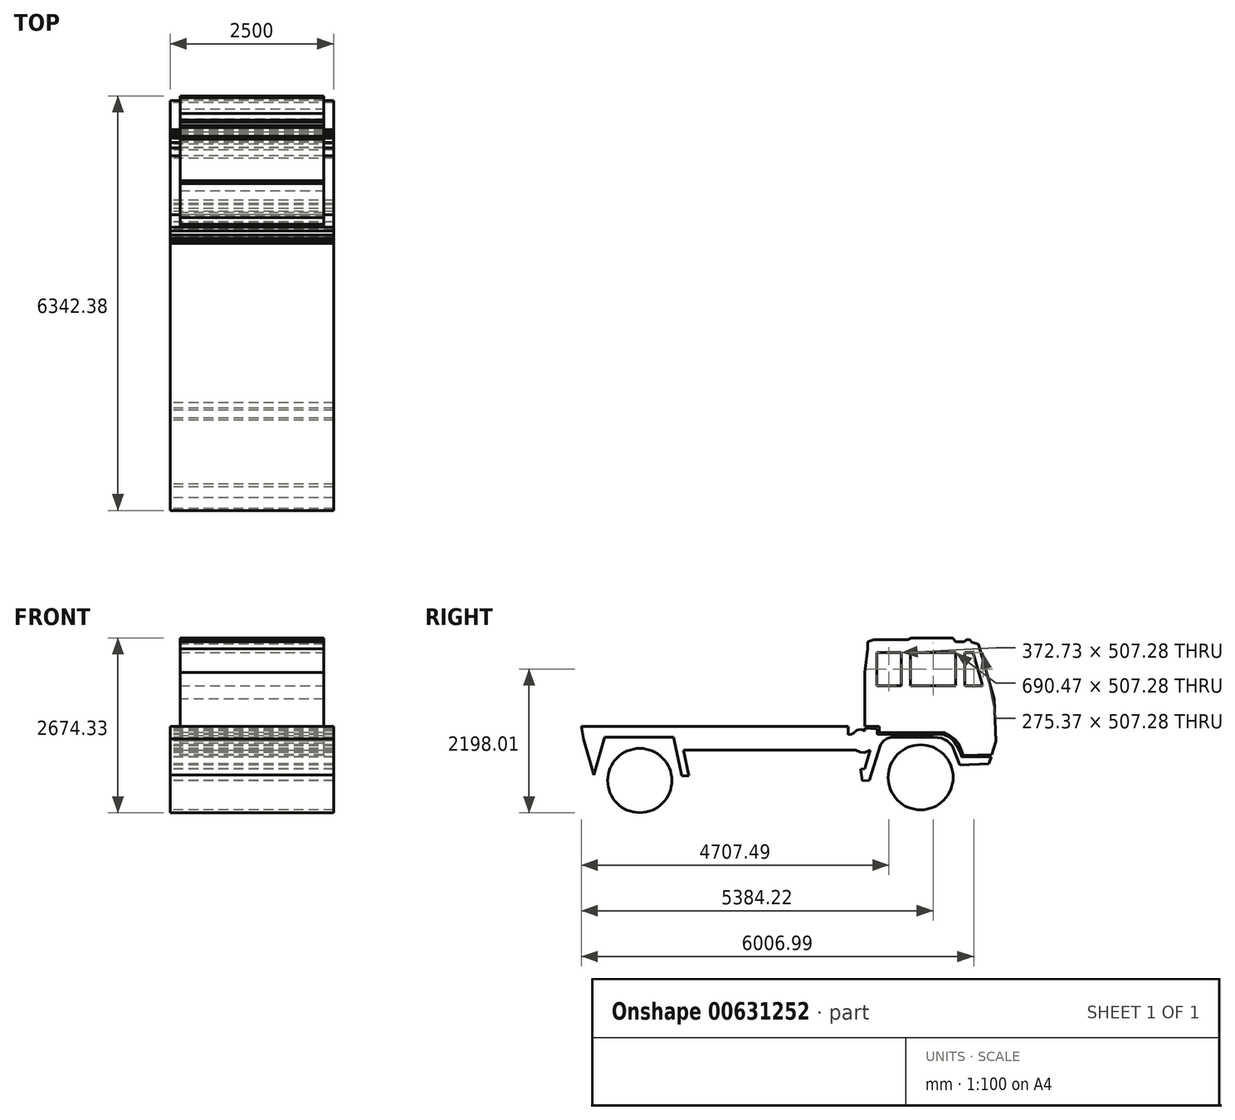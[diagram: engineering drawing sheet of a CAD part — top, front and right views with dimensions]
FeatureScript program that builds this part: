
annotation { "Feature Type Name" : "Feature", "Feature Type Description" : "" }
export const myFeature = defineFeature(function(context is Context, id is Id, definition is map)
    precondition{}
    {
        {
            var Q0;
            Q0=qCreatedBy(makeId("Right.planeOp"),FACE);
            var sketch = newSketch(context, id + "F0", { "sketchPlane" : qUnion([Q0])});
            skLineSegment(sketch, "E0", {"start": v(53.1, 1349.44) * mm, "end": v(53.1, -1350.56) * mm, "construction": true});
            skLineSegment(sketch, "E1", {"start": v(-5310.61, 0) * mm, "end": v(-1224.55, 0) * mm});
            skLineSegment(sketch, "E2", {"start": v(-1224.55, 0) * mm, "end": v(-1224.55, -122.4) * mm});
            skLineSegment(sketch, "E3", {"start": v(-5277.76, -191.96) * mm, "end": v(-5310.61, 0) * mm});
            skLineSegment(sketch, "E4", {"start": v(-974.86, -69.75) * mm, "end": v(-1031.73, -44.93) * mm});
            skLineSegment(sketch, "E5", {"start": v(-1031.73, -44.93) * mm, "end": v(-1096.05, -56.42) * mm});
            skLineSegment(sketch, "E6", {"start": v(-1096.05, -56.42) * mm, "end": v(-1148.89, -109.25) * mm});
            skLineSegment(sketch, "E7", {"start": v(-1148.89, -109.25) * mm, "end": v(-1181.05, -120.74) * mm});
            skLineSegment(sketch, "E8", {"start": v(-1181.05, -120.74) * mm, "end": v(-1224.55, -122.4) * mm});
            skLineSegment(sketch, "E9", {"start": v(962.07, -459.7) * mm, "end": v(927, -569.93) * mm});
            skLineSegment(sketch, "E10", {"start": v(927, -569.93) * mm, "end": v(478.37, -587.13) * mm});
            skLineSegment(sketch, "E11", {"start": v(478.37, -587.13) * mm, "end": v(369.28, -296.74) * mm});
            skLineSegment(sketch, "E12", {"start": v(369.28, -296.74) * mm, "end": v(293.2, -219.28) * mm});
            skLineSegment(sketch, "E13", {"start": v(293.2, -219.28) * mm, "end": v(203.83, -177.57) * mm});
            skLineSegment(sketch, "E14", {"start": v(203.83, -177.57) * mm, "end": v(75.64, -166.68) * mm});
            skLineSegment(sketch, "E15", {"start": v(75.64, -166.68) * mm, "end": v(-564.8, -166.68) * mm});
            skLineSegment(sketch, "E16", {"start": v(-564.8, -166.68) * mm, "end": v(-630.34, -180.55) * mm});
            skLineSegment(sketch, "E17", {"start": v(-630.34, -180.55) * mm, "end": v(-686.95, -222.26) * mm});
            skLineSegment(sketch, "E18", {"start": v(-686.95, -222.26) * mm, "end": v(-731.63, -278.87) * mm});
            skLineSegment(sketch, "E19", {"start": v(-731.63, -278.87) * mm, "end": v(-900.62, -823.83) * mm});
            skLineSegment(sketch, "E20", {"start": v(-900.62, -823.83) * mm, "end": v(-1012.8, -828.13) * mm});
            skLineSegment(sketch, "E21", {"start": v(-1012.8, -828.13) * mm, "end": v(-1035.85, -653.83) * mm});
            skLineSegment(sketch, "E22", {"start": v(-1035.85, -653.83) * mm, "end": v(-974.86, -645.77) * mm});
            skLineSegment(sketch, "E23", {"start": v(-974.86, -645.77) * mm, "end": v(-892.9, -360.2) * mm});
            skLineSegment(sketch, "E24", {"start": v(-892.9, -360.2) * mm, "end": v(-974.86, -398.84) * mm});
            skLineSegment(sketch, "E25", {"start": v(-974.86, -398.84) * mm, "end": v(-1040.88, -393.23) * mm});
            skLineSegment(sketch, "E26", {"start": v(-1040.88, -393.23) * mm, "end": v(-1113.12, -360.2) * mm});
            skLineSegment(sketch, "E27", {"start": v(-1113.12, -360.2) * mm, "end": v(-3746.88, -360.2) * mm});
            skLineSegment(sketch, "E28", {"start": v(-3746.88, -360.2) * mm, "end": v(-3663.76, -753.07) * mm});
            skLineSegment(sketch, "E29", {"start": v(-3663.76, -753.07) * mm, "end": v(-3775.22, -753.07) * mm});
            skLineSegment(sketch, "E30", {"start": v(-3775.22, -753.07) * mm, "end": v(-3899.29, -166.68) * mm});
            skLineSegment(sketch, "E31", {"start": v(-3899.29, -166.68) * mm, "end": v(-4951.76, -166.68) * mm});
            skLineSegment(sketch, "E32", {"start": v(-4951.76, -166.68) * mm, "end": v(-5117.41, -743.82) * mm});
            skLineSegment(sketch, "E33", {"start": v(-5117.41, -743.82) * mm, "end": v(-5277.76, -191.96) * mm});
            skLineSegment(sketch, "E34", {"start": v(-974.86, -24.33) * mm, "end": v(-782.84, -37.54) * mm});
            skLineSegment(sketch, "E35", {"start": v(-782.84, -37.54) * mm, "end": v(-782.84, -116.8) * mm});
            skLineSegment(sketch, "E36", {"start": v(-782.84, -116.8) * mm, "end": v(119.62, -116.8) * mm});
            skLineSegment(sketch, "E37", {"start": v(119.62, -116.8) * mm, "end": v(239.29, -125.04) * mm});
            skLineSegment(sketch, "E38", {"start": v(239.29, -125.04) * mm, "end": v(321.4, -166.68) * mm});
            skLineSegment(sketch, "E39", {"start": v(321.4, -166.68) * mm, "end": v(388.67, -216.02) * mm});
            skLineSegment(sketch, "E40", {"start": v(388.67, -216.02) * mm, "end": v(433.51, -283.28) * mm});
            skLineSegment(sketch, "E41", {"start": v(433.51, -283.28) * mm, "end": v(478.35, -380.44) * mm});
            skLineSegment(sketch, "E42", {"start": v(478.35, -380.44) * mm, "end": v(515.72, -470.12) * mm});
            skLineSegment(sketch, "E43", {"start": v(515.72, -470.12) * mm, "end": v(962.07, -459.7) * mm});
            skLineSegment(sketch, "E44", {"start": v(-974.86, -24.33) * mm, "end": v(-974.86, -69.75) * mm});
            skSolve(sketch);
        }
        {
            var Q0;
            Q0=makeQuery(id+"F0.imprint","IMPRINT",FACE,{"disambiguationData":[TD([[makeQuery(id+"F0.imprint","IMPRINT",EDGE,{"derivedFrom":sQuery(id+"F0.wireOp",EDGE,"E1")}),-1.0]])]});
            var sketch = newSketch(context, id + "F1", { "sketchPlane" : qUnion([Q0])});
            skCircle(sketch, "E45", {"center": v(-4416.91, -827.06) * mm, "radius": 491.64 * mm});
            skCircle(sketch, "E46", {"center": v(-118.33, -776.78) * mm, "radius": 498.02 * mm});
            skSolve(sketch);
        }
        {
            var Q0;
            Q0=makeQuery(id+"F0.imprint","IMPRINT",FACE,{"disambiguationData":[TD([[makeQuery(id+"F0.imprint","IMPRINT",EDGE,{"derivedFrom":sQuery(id+"F0.wireOp",EDGE,"E1")}),-1.0]])]});
            var sketch = newSketch(context, id + "F2", { "sketchPlane" : qUnion([Q0])});
            skLineSegment(sketch, "E47", {"start": v(-974.57, 0) * mm, "end": v(-974.57, 829.4) * mm});
            skLineSegment(sketch, "E48", {"start": v(-974.57, 829.4) * mm, "end": v(-929.28, 1191.21) * mm});
            skLineSegment(sketch, "E49", {"start": v(-929.28, 1191.21) * mm, "end": v(-929.28, 1295.84) * mm});
            skLineSegment(sketch, "E50", {"start": v(-929.28, 1295.84) * mm, "end": v(-832.13, 1325.74) * mm});
            skLineSegment(sketch, "E51", {"start": v(-832.13, 1325.74) * mm, "end": v(-308.98, 1325.74) * mm});
            skLineSegment(sketch, "E52", {"start": v(-308.98, 1325.74) * mm, "end": v(-264.14, 1355.63) * mm});
            skLineSegment(sketch, "E53", {"start": v(-264.14, 1355.63) * mm, "end": v(371.12, 1355.63) * mm});
            skLineSegment(sketch, "E54", {"start": v(371.12, 1355.63) * mm, "end": v(415.96, 1295.84) * mm});
            skLineSegment(sketch, "E55", {"start": v(415.96, 1295.84) * mm, "end": v(550.48, 1295.84) * mm});
            skLineSegment(sketch, "E56", {"start": v(550.48, 1295.84) * mm, "end": v(580.38, 1325.74) * mm});
            skLineSegment(sketch, "E57", {"start": v(580.38, 1325.74) * mm, "end": v(632.7, 1325.74) * mm});
            skLineSegment(sketch, "E58", {"start": v(632.7, 1325.74) * mm, "end": v(662.59, 1288.37) * mm});
            skLineSegment(sketch, "E59", {"start": v(662.59, 1288.37) * mm, "end": v(767.21, 1258.48) * mm});
            skLineSegment(sketch, "E60", {"start": v(767.21, 1258.48) * mm, "end": v(1006.37, 421.44) * mm});
            skLineSegment(sketch, "E61", {"start": v(1006.37, 421.44) * mm, "end": v(1031.77, -227.26) * mm});
            skLineSegment(sketch, "E62", {"start": v(1031.77, -227.26) * mm, "end": v(968.38, -428.96) * mm});
            skLineSegment(sketch, "E63", {"start": v(968.38, -428.96) * mm, "end": v(533.98, -442.83) * mm});
            skLineSegment(sketch, "E64", {"start": v(533.98, -442.83) * mm, "end": v(506.57, -364.01) * mm});
            skLineSegment(sketch, "E65", {"start": v(506.57, -364.01) * mm, "end": v(462.02, -261.21) * mm});
            skLineSegment(sketch, "E66", {"start": v(462.02, -261.21) * mm, "end": v(403.77, -192.68) * mm});
            skLineSegment(sketch, "E67", {"start": v(403.77, -192.68) * mm, "end": v(335.24, -144.7) * mm});
            skLineSegment(sketch, "E68", {"start": v(335.24, -144.7) * mm, "end": v(246.15, -93.3) * mm});
            skLineSegment(sketch, "E69", {"start": v(246.15, -93.3) * mm, "end": v(119.36, -93.3) * mm});
            skLineSegment(sketch, "E70", {"start": v(119.36, -93.3) * mm, "end": v(-750.7, -93.3) * mm});
            skLineSegment(sketch, "E71", {"start": v(-750.7, -93.3) * mm, "end": v(-750.7, 0) * mm});
            skLineSegment(sketch, "E72", {"start": v(-750.7, 0) * mm, "end": v(-974.57, 0) * mm});
            skSolve(sketch);
        }
        {
            var Q0;
            Q0=makeQuery(id+"F0.imprint","IMPRINT",FACE,{"disambiguationData":[TD([[makeQuery(id+"F0.imprint","IMPRINT",EDGE,{"derivedFrom":sQuery(id+"F0.wireOp",EDGE,"E1")}),-1.0]])]});
            extrude(context, id + "F3", {"entities" : qUnion([Q0]), "depth" : 2500 * mm, "offsetDistance" : 25 * mm});
        }
        {
            var Q0;
            Q0=makeQuery(id+"F2.imprint","IMPRINT",FACE,{"disambiguationData":[TD([[makeQuery(id+"F2.imprint","IMPRINT",EDGE,{"derivedFrom":sQuery(id+"F2.wireOp",EDGE,"E47")}),-1.0]])]});
            extrude(context, id + "F4", {"entities" : qUnion([Q0]), "depth" : 2500 * mm, "offsetDistance" : 25 * mm});
        }
        {
            var Q0;
            Q0=makeQuery(id+"F1.imprint","IMPRINT",FACE,{"disambiguationData":[TD([[makeQuery(id+"F1.imprint","IMPRINT",EDGE,{"derivedFrom":sQuery(id+"F1.wireOp",EDGE,"E45")}),1.0]])]});
            var Q1;
            Q1=makeQuery(id+"F1.imprint","IMPRINT",FACE,{"disambiguationData":[TD([[makeQuery(id+"F1.imprint","IMPRINT",EDGE,{"derivedFrom":sQuery(id+"F1.wireOp",EDGE,"E46")}),1.0]])]});
            extrude(context, id + "F5", {"entities" : qUnion([Q0, Q1]), "depth" : 2500 * mm, "offsetDistance" : 25 * mm});
        }
        {
            var Q0;
            Q0=makeQuery(id+"F4.opExtrude","CAP_FACE",FACE,{"disambiguationData":[OSD([sQuery(id+"F2.wireOp",EDGE,"E47"),sQuery(id+"F2.wireOp",EDGE,"E48"),sQuery(id+"F2.wireOp",EDGE,"E49"),sQuery(id+"F2.wireOp",EDGE,"E50"),sQuery(id+"F2.wireOp",EDGE,"E51"),sQuery(id+"F2.wireOp",EDGE,"E52"),sQuery(id+"F2.wireOp",EDGE,"E53"),sQuery(id+"F2.wireOp",EDGE,"E54"),sQuery(id+"F2.wireOp",EDGE,"E55"),sQuery(id+"F2.wireOp",EDGE,"E56"),sQuery(id+"F2.wireOp",EDGE,"E57"),sQuery(id+"F2.wireOp",EDGE,"E58"),sQuery(id+"F2.wireOp",EDGE,"E59"),sQuery(id+"F2.wireOp",EDGE,"E60"),sQuery(id+"F2.wireOp",EDGE,"E61"),sQuery(id+"F2.wireOp",EDGE,"E62"),sQuery(id+"F2.wireOp",EDGE,"E63"),sQuery(id+"F2.wireOp",EDGE,"E64"),sQuery(id+"F2.wireOp",EDGE,"E65"),sQuery(id+"F2.wireOp",EDGE,"E66"),sQuery(id+"F2.wireOp",EDGE,"E67"),sQuery(id+"F2.wireOp",EDGE,"E68"),sQuery(id+"F2.wireOp",EDGE,"E69"),sQuery(id+"F2.wireOp",EDGE,"E70"),sQuery(id+"F2.wireOp",EDGE,"E71"),sQuery(id+"F2.wireOp",EDGE,"E72")])],"isStart":false});
            var sketch = newSketch(context, id + "F6", { "sketchPlane" : qUnion([Q0])});
            skLineSegment(sketch, "E73.bottom", {"start": v(-789.49, 1132.95) * mm, "end": v(-416.75, 1132.95) * mm});
            skLineSegment(sketch, "E73.top", {"start": v(-789.49, 625.67) * mm, "end": v(-416.75, 625.67) * mm});
            skLineSegment(sketch, "E73.left", {"start": v(-789.49, 1132.95) * mm, "end": v(-789.49, 625.67) * mm});
            skLineSegment(sketch, "E73.right", {"start": v(-416.75, 1132.95) * mm, "end": v(-416.75, 625.67) * mm});
            skLineSegment(sketch, "E74.bottom", {"start": v(-271.63, 1132.95) * mm, "end": v(418.84, 1132.95) * mm});
            skLineSegment(sketch, "E74.top", {"start": v(-271.63, 625.67) * mm, "end": v(418.84, 625.67) * mm});
            skLineSegment(sketch, "E74.left", {"start": v(-271.63, 1132.95) * mm, "end": v(-271.63, 625.67) * mm});
            skLineSegment(sketch, "E74.right", {"start": v(418.84, 1132.95) * mm, "end": v(418.84, 625.67) * mm});
            skLineSegment(sketch, "E75", {"start": v(558.7, 1132.95) * mm, "end": v(558.7, 625.67) * mm});
            skPoint(sketch, "E75.startSnap0", {"position": v(-603.12, 1132.95) * mm});
            skLineSegment(sketch, "E76", {"start": v(558.7, 625.67) * mm, "end": v(834.06, 625.67) * mm});
            skLineSegment(sketch, "E77", {"start": v(834.06, 625.67) * mm, "end": v(681.77, 1132.95) * mm});
            skLineSegment(sketch, "E78", {"start": v(681.77, 1132.95) * mm, "end": v(558.7, 1132.95) * mm});
            skSolve(sketch);
        }
        {
            var Q0;
            Q0=makeQuery(id+"F6.imprint","IMPRINT",FACE,{"disambiguationData":[TD([[makeQuery(id+"F6.imprint","IMPRINT",EDGE,{"derivedFrom":sQuery(id+"F6.wireOp",EDGE,"E73.bottom")}),-1.0]])]});
            var Q1;
            Q1=makeQuery(id+"F6.imprint","IMPRINT",FACE,{"disambiguationData":[TD([[makeQuery(id+"F6.imprint","IMPRINT",EDGE,{"derivedFrom":sQuery(id+"F6.wireOp",EDGE,"E74.bottom")}),-1.0]])]});
            var Q2;
            Q2=makeQuery(id+"F6.imprint","IMPRINT",FACE,{"disambiguationData":[TD([[makeQuery(id+"F6.imprint","IMPRINT",EDGE,{"derivedFrom":sQuery(id+"F6.wireOp",EDGE,"E75")}),1.0]])]});
            extrude(context, id + "F7", {"entities" : qUnion([Q0, Q1, Q2]), "operationType" : NewBodyOperationType.REMOVE, "endBound" : BoundingType.UP_TO_NEXT, "oppositeDirection" : true, "depth" : 250 * mm, "offsetDistance" : 25 * mm});
        }
        {
            var Q0;
            Q0=makeQuery(id+"F4.opExtrude","CAP_FACE",FACE,{"disambiguationData":[OSD([sQuery(id+"F2.wireOp",EDGE,"E47"),sQuery(id+"F2.wireOp",EDGE,"E48"),sQuery(id+"F2.wireOp",EDGE,"E49"),sQuery(id+"F2.wireOp",EDGE,"E50"),sQuery(id+"F2.wireOp",EDGE,"E51"),sQuery(id+"F2.wireOp",EDGE,"E52"),sQuery(id+"F2.wireOp",EDGE,"E53"),sQuery(id+"F2.wireOp",EDGE,"E54"),sQuery(id+"F2.wireOp",EDGE,"E55"),sQuery(id+"F2.wireOp",EDGE,"E56"),sQuery(id+"F2.wireOp",EDGE,"E57"),sQuery(id+"F2.wireOp",EDGE,"E58"),sQuery(id+"F2.wireOp",EDGE,"E59"),sQuery(id+"F2.wireOp",EDGE,"E60"),sQuery(id+"F2.wireOp",EDGE,"E61"),sQuery(id+"F2.wireOp",EDGE,"E62"),sQuery(id+"F2.wireOp",EDGE,"E63"),sQuery(id+"F2.wireOp",EDGE,"E64"),sQuery(id+"F2.wireOp",EDGE,"E65"),sQuery(id+"F2.wireOp",EDGE,"E66"),sQuery(id+"F2.wireOp",EDGE,"E67"),sQuery(id+"F2.wireOp",EDGE,"E68"),sQuery(id+"F2.wireOp",EDGE,"E69"),sQuery(id+"F2.wireOp",EDGE,"E70"),sQuery(id+"F2.wireOp",EDGE,"E71"),sQuery(id+"F2.wireOp",EDGE,"E72")])],"isStart":false});
            extrude(context, id + "F8", {"entities" : qUnion([Q0]), "operationType" : NewBodyOperationType.REMOVE, "oppositeDirection" : true, "depth" : 150 * mm, "offsetDistance" : 25 * mm});
        }
        {
            var Q0;
            Q0=makeQuery(id+"F4.opExtrude","CAP_FACE",FACE,{"disambiguationData":[OSD([sQuery(id+"F2.wireOp",EDGE,"E47"),sQuery(id+"F2.wireOp",EDGE,"E48"),sQuery(id+"F2.wireOp",EDGE,"E49"),sQuery(id+"F2.wireOp",EDGE,"E50"),sQuery(id+"F2.wireOp",EDGE,"E51"),sQuery(id+"F2.wireOp",EDGE,"E52"),sQuery(id+"F2.wireOp",EDGE,"E53"),sQuery(id+"F2.wireOp",EDGE,"E54"),sQuery(id+"F2.wireOp",EDGE,"E55"),sQuery(id+"F2.wireOp",EDGE,"E56"),sQuery(id+"F2.wireOp",EDGE,"E57"),sQuery(id+"F2.wireOp",EDGE,"E58"),sQuery(id+"F2.wireOp",EDGE,"E59"),sQuery(id+"F2.wireOp",EDGE,"E60"),sQuery(id+"F2.wireOp",EDGE,"E61"),sQuery(id+"F2.wireOp",EDGE,"E62"),sQuery(id+"F2.wireOp",EDGE,"E63"),sQuery(id+"F2.wireOp",EDGE,"E64"),sQuery(id+"F2.wireOp",EDGE,"E65"),sQuery(id+"F2.wireOp",EDGE,"E66"),sQuery(id+"F2.wireOp",EDGE,"E67"),sQuery(id+"F2.wireOp",EDGE,"E68"),sQuery(id+"F2.wireOp",EDGE,"E69"),sQuery(id+"F2.wireOp",EDGE,"E70"),sQuery(id+"F2.wireOp",EDGE,"E71"),sQuery(id+"F2.wireOp",EDGE,"E72")])],"isStart":true});
            extrude(context, id + "F9", {"entities" : qUnion([Q0]), "operationType" : NewBodyOperationType.REMOVE, "oppositeDirection" : true, "depth" : 150 * mm, "offsetDistance" : 25 * mm});
        }
    });
